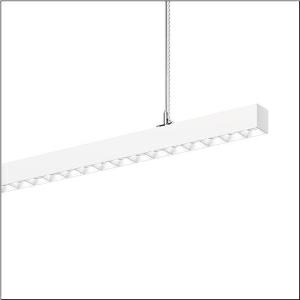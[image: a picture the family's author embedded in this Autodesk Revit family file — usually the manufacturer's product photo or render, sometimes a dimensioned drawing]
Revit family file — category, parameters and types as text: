
# Revit family: silica_21_51mx36da37wb
name_source: partatom
category: Lighting Fixtures
units: mm (PartAtom-declared; Revit-internal decimal feet)

## family parameters
Cut with Voids When Loaded = No
Host = Face
Light Source = No
Part Type = Normal
Room Calculation Point = No
Round Connector Dimension = Use Diameter
Shared = No

## types (1)
- --- (1 x LED, 7060 lm, 43 W, 3000K)
    Apparent Load = 43 VA
    CIE Flux Codes = 83 98 100 61 100
    Color Rendering = 80
    Color Temperature = 3000K
    Default Elevation = 1800 mm
    Description = Silica 21, office luminaire, primary light control with darklight reflector, of PMMA, white, CAT 2 (L<= 3000cd/m²), light emission: direct/indirect distribution, primary light characteristic: symmetric, installation type: suspended mounting, LED, rated luminous flux: 7.060lm, luminous efficacy: 164lm/W, light colour: 830, colour temperature: 3000K, control gear: DALI 2, with terminal, 3+2-pole, max. 2.5mm², mains connection: 220..240V, AC, 50/60Hz, rated input power: 43W, luminaire housing, of aluminium, traffic white (RAL 9016), length: 1.204mm, width: 53mm, height: 53mm, protection rating (complete): IP20, insulation class (complete): insulation class I (protective earthing), certification: CE, permissible operating ambient temperature: 0..+35°C, standard: EN 50419, packaging unit: 1 piece
    Height = 53 mm
    Lamp = 1 x LED
    Lamp Light Flux = 7060 lm
    Lamp Power = 43 W
    Lamp count = 1
    Length = 1204 mm
    Luminous efficacy = 164 lm/W
    Manufacturer = Siteco
    ModVariant = No
    Model = 51MX36DA37WB
    Mounting Place = Ceiling
    Mounting Type = Pendant
    Number of Poles = 1
    OnlyDefault = Yes
    Power Factor = 1
    Product Name = Silica 21
    Product group = office luminaire | ceiling pendant
    ProductGroupID = 903
    Protection Class = Protection class I
    Protection Degree = IP 20
    RLX_Detail_Level = 1
    RLX_Emergency_Light_Flux = 0 lm
    RLX_Emergency_Type = 0
    RLX_Emergency_Type_DB = No
    RlxData = <blob elided: 40561 chars, md5=94815d35>
    Socket = socket
    Standby Power = 0 W
    System Light Flux = 7060 lm
    System Power = 43 W
    Type Comments = factory setting: luminous flux: 100 % | dim-lin: 254 | 359 mA
    Type Image = l_1335921.jpg
    URL = http://relux.com
    VarID = @adj_123077
    Voltage = 0 V
    Weight = 0.00 kg
    Width = 53 mm

## geometry (parser evidence)
native form markers: Blend x4, Sweep x11
no freeform markers — native parametric forms only
